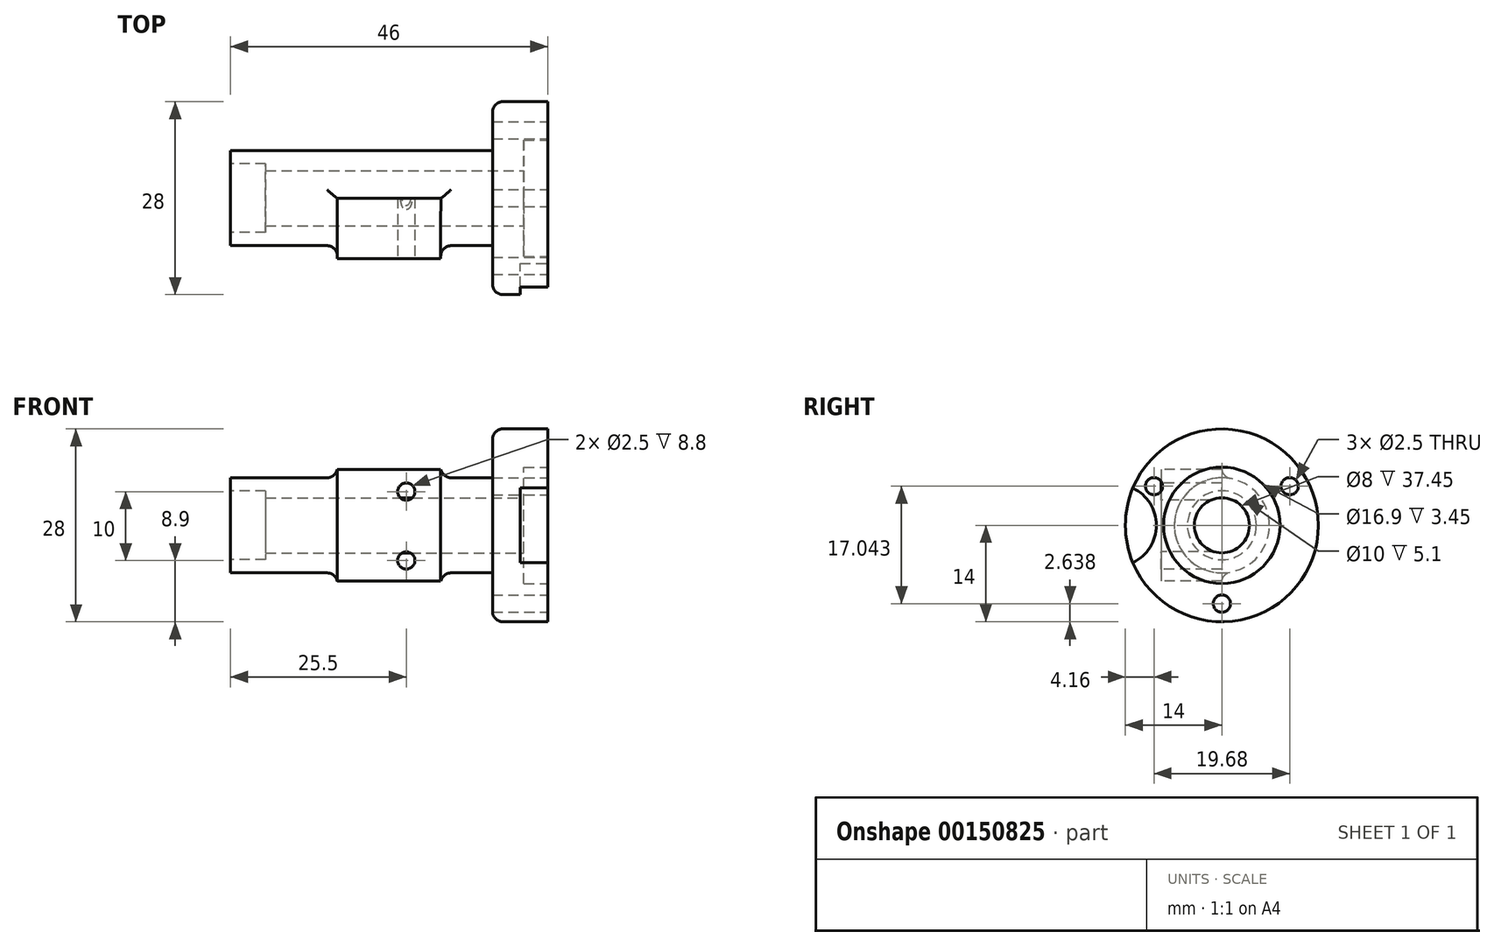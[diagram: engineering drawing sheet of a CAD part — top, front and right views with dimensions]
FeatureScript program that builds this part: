
annotation { "Feature Type Name" : "Feature", "Feature Type Description" : "" }
export const myFeature = defineFeature(function(context is Context, id is Id, definition is map)
    precondition{}
    {
        {
            var Q0;
            Q0=qCreatedBy(makeId("Right.planeOp"),FACE);
            var sketch = newSketch(context, id + "F0", { "sketchPlane" : qUnion([Q0])});
            skCircle(sketch, "E0", {"center": v(0, 0) * mm, "radius": 14 * mm});
            skSolve(sketch);
        }
        {
            var Q0;
            Q0=makeQuery(id+"F0.imprint","IMPRINT",FACE,{"disambiguationData":[TD([[makeQuery(id+"F0.imprint","IMPRINT",EDGE,{"derivedFrom":sQuery(id+"F0.wireOp",EDGE,"E0")}),1.0]])]});
            extrude(context, id + "F1", {"entities" : qUnion([Q0]), "depth" : 8 * mm});
        }
        {
            var Q0;
            Q0=makeQuery(id+"F1.opExtrude","CAP_FACE",FACE,{"disambiguationData":[OSD([sQuery(id+"F0.wireOp",EDGE,"E0")])],"isStart":false});
            var sketch = newSketch(context, id + "F2", { "sketchPlane" : qUnion([Q0])});
            skCircle(sketch, "E1", {"center": v(0, 0) * mm, "radius": 8.45 * mm});
            skSolve(sketch);
        }
        {
            var Q0;
            Q0=qSketchRegion(id+"F2",true);
            extrude(context, id + "F3", {"entities" : qUnion([Q0]), "operationType" : NewBodyOperationType.REMOVE, "oppositeDirection" : true, "depth" : 3.45 * mm});
        }
        {
            var Q0;
            Q0=makeQuery(id+"F1.opExtrude","CAP_FACE",FACE,{"disambiguationData":[OSD([sQuery(id+"F0.wireOp",EDGE,"E0")])],"isStart":false});
            var sketch = newSketch(context, id + "F4", { "sketchPlane" : qUnion([Q0])});
            skCircle(sketch, "E2", {"center": v(0, 0) * mm, "radius": 11.36 * mm, "construction": true});
            skCircle(sketch, "E3", {"center": v(0, -11.36) * mm, "radius": 1.25 * mm});
            skCircle(sketch, "E4.1.0", {"center": v(9.84, 5.68) * mm, "radius": 1.25 * mm});
            skCircle(sketch, "E4.2.0", {"center": v(-9.84, 5.68) * mm, "radius": 1.25 * mm});
            skSolve(sketch);
        }
        {
            var Q0;
            Q0=makeQuery(id+"F4.imprint","IMPRINT",FACE,{"disambiguationData":[TD([[makeQuery(id+"F4.imprint","IMPRINT",EDGE,{"derivedFrom":sQuery(id+"F4.wireOp",EDGE,"E4.2.0")}),1.0]])]});
            var Q1;
            Q1=makeQuery(id+"F4.imprint","IMPRINT",FACE,{"disambiguationData":[TD([[makeQuery(id+"F4.imprint","IMPRINT",EDGE,{"derivedFrom":sQuery(id+"F4.wireOp",EDGE,"E4.1.0")}),1.0]])]});
            var Q2;
            Q2=makeQuery(id+"F4.imprint","IMPRINT",FACE,{"disambiguationData":[TD([[makeQuery(id+"F4.imprint","IMPRINT",EDGE,{"derivedFrom":sQuery(id+"F4.wireOp",EDGE,"E3")}),1.0]])]});
            extrude(context, id + "F5", {"entities" : qUnion([Q0, Q1, Q2]), "operationType" : NewBodyOperationType.REMOVE, "endBound" : BoundingType.THROUGH_ALL, "oppositeDirection" : true, "depth" : 25 * mm});
        }
        {
            var Q0;
            Q0=makeQuery(id+"F1.opExtrude","CAP_FACE",FACE,{"disambiguationData":[OSD([sQuery(id+"F0.wireOp",EDGE,"E0")])],"isStart":true});
            var sketch = newSketch(context, id + "F6", { "sketchPlane" : qUnion([Q0])});
            skCircle(sketch, "E5", {"center": v(0, 0) * mm, "radius": 6.9 * mm});
            skSolve(sketch);
        }
        {
            var Q0;
            Q0=makeQuery(id+"F6.imprint","IMPRINT",FACE,{"disambiguationData":[TD([[makeQuery(id+"F6.imprint","IMPRINT",EDGE,{"derivedFrom":sQuery(id+"F6.wireOp",EDGE,"E5")}),1.0]])]});
            extrude(context, id + "F7", {"entities" : qUnion([Q0]), "operationType" : NewBodyOperationType.ADD, "depth" : 38 * mm});
        }
        {
            var Q0;
            Q0=qCreatedBy(makeId("Top.planeOp"),FACE);
            var sketch = newSketch(context, id + "F8", { "sketchPlane" : qUnion([Q0])});
            skLineSegment(sketch, "E6.bottom", {"start": v(-22.5, 0) * mm, "end": v(-7.5, 0) * mm});
            skLineSegment(sketch, "E6.top", {"start": v(-22.5, -8.8) * mm, "end": v(-7.5, -8.8) * mm});
            skLineSegment(sketch, "E6.left", {"start": v(-22.5, 0) * mm, "end": v(-22.5, -8.8) * mm});
            skLineSegment(sketch, "E6.right", {"start": v(-7.5, 0) * mm, "end": v(-7.5, -8.8) * mm});
            skSolve(sketch);
        }
        {
            var Q0;
            Q0=makeQuery(id+"F8.imprint","IMPRINT",FACE,{"disambiguationData":[TD([[makeQuery(id+"F8.imprint","IMPRINT",EDGE,{"derivedFrom":sQuery(id+"F8.wireOp",EDGE,"E6.bottom")}),-1.0]])]});
            extrude(context, id + "F9", {"entities" : qUnion([Q0]), "operationType" : NewBodyOperationType.ADD, "endBound" : BoundingType.SYMMETRIC, "depth" : 16.2 * mm});
        }
        {
            var Q0;
            Q0=makeQuery(id+"F1.opExtrude","CAP_FACE",FACE,{"disambiguationData":[OSD([sQuery(id+"F0.wireOp",EDGE,"E0")])],"isStart":false});
            var sketch = newSketch(context, id + "F10", { "sketchPlane" : qUnion([Q0])});
            skCircle(sketch, "E7", {"center": v(0, 0) * mm, "radius": 4 * mm});
            skSolve(sketch);
        }
        {
            var Q0;
            Q0=makeQuery(id+"F10.imprint","IMPRINT",FACE,{"disambiguationData":[TD([[makeQuery(id+"F10.imprint","IMPRINT",EDGE,{"derivedFrom":sQuery(id+"F10.wireOp",EDGE,"E7")}),1.0]])]});
            extrude(context, id + "F11", {"entities" : qUnion([Q0]), "operationType" : NewBodyOperationType.REMOVE, "endBound" : BoundingType.THROUGH_ALL, "oppositeDirection" : true, "depth" : 25 * mm});
        }
        {
            var Q0;
            Q0=makeQuery(id+"F7.opExtrude","CAP_FACE",FACE,{"disambiguationData":[OSD([sQuery(id+"F6.wireOp",EDGE,"E5")])],"isStart":false});
            var sketch = newSketch(context, id + "F12", { "sketchPlane" : qUnion([Q0])});
            skCircle(sketch, "E8", {"center": v(0, 0) * mm, "radius": 5 * mm});
            skSolve(sketch);
        }
        {
            var Q0;
            Q0=makeQuery(id+"F12.imprint","IMPRINT",FACE,{"disambiguationData":[TD([[makeQuery(id+"F12.imprint","IMPRINT",EDGE,{"derivedFrom":sQuery(id+"F12.wireOp",EDGE,"E8")}),1.0]])]});
            extrude(context, id + "F13", {"entities" : qUnion([Q0]), "operationType" : NewBodyOperationType.REMOVE, "oppositeDirection" : true, "depth" : 5.1 * mm});
        }
        {
            var Q0;
            Q0=makeQuery(id+"F9.opExtrude","SWEPT_FACE",FACE,{"disambiguationData":[OSD([sQuery(id+"F8.wireOp",EDGE,"E6.top")])]});
            var sketch = newSketch(context, id + "F14", { "sketchPlane" : qUnion([Q0])});
            skCircle(sketch, "E9", {"center": v(-12.5, -5.1) * mm, "radius": 1.25 * mm});
            skLineSegment(sketch, "E10", {"start": v(-12.5, -16.17) * mm, "end": v(-12.5, 16.97) * mm, "construction": true});
            skCircle(sketch, "E11", {"center": v(-12.5, 4.9) * mm, "radius": 1.25 * mm});
            skSolve(sketch);
        }
        {
            var Q0;
            Q0=makeQuery(id+"F14.imprint","IMPRINT",FACE,{"disambiguationData":[TD([[makeQuery(id+"F14.imprint","IMPRINT",EDGE,{"derivedFrom":sQuery(id+"F14.wireOp",EDGE,"E11")}),1.0]])]});
            var Q1;
            Q1=makeQuery(id+"F14.imprint","IMPRINT",FACE,{"disambiguationData":[TD([[makeQuery(id+"F14.imprint","IMPRINT",EDGE,{"derivedFrom":sQuery(id+"F14.wireOp",EDGE,"E9")}),1.0]])]});
            extrude(context, id + "F15", {"entities" : qUnion([Q0, Q1]), "operationType" : NewBodyOperationType.REMOVE, "oppositeDirection" : true, "depth" : 8.8 * mm});
        }
        {
            var Q0;
            Q0=makeQuery(id+"F1.opExtrude","CAP_FACE",FACE,{"disambiguationData":[OSD([sQuery(id+"F0.wireOp",EDGE,"E0")])],"isStart":false});
            var sketch = newSketch(context, id + "F16", { "sketchPlane" : qUnion([Q0])});
            skCircle(sketch, "E12", {"center": v(-15.5, 0) * mm, "radius": 6 * mm});
            skSolve(sketch);
        }
        {
            var Q0;
            Q0=qSketchRegion(id+"F16",true);
            extrude(context, id + "F17", {"entities" : qUnion([Q0]), "operationType" : NewBodyOperationType.REMOVE, "oppositeDirection" : true, "depth" : 4 * mm});
        }
        {
            var Q0;
            Q0=makeQuery(id+"F7.opExtrude","CAP_EDGE",EDGE,{"disambiguationData":[OSD([sQuery(id+"F6.wireOp",EDGE,"E5")])],"isStart":true});
            var Q1;
            Q1=makeQuery(id+"F9.boolean.opBoolean","INTERSECT",EDGE,{"derivedFrom":[makeQuery(id+"F7.opExtrude","SWEPT_FACE",FACE,{"disambiguationData":[OSD([sQuery(id+"F6.wireOp",EDGE,"E5")])]}),makeQuery(id+"F9.opExtrude","SWEPT_FACE",FACE,{"disambiguationData":[OSD([sQuery(id+"F8.wireOp",EDGE,"E6.left")])]})]});
            var Q2;
            Q2=makeQuery(id+"F9.boolean.opBoolean","INTERSECT",EDGE,{"derivedFrom":[makeQuery(id+"F7.opExtrude","SWEPT_FACE",FACE,{"disambiguationData":[OSD([sQuery(id+"F6.wireOp",EDGE,"E5")])]}),makeQuery(id+"F9.opExtrude","SWEPT_FACE",FACE,{"disambiguationData":[OSD([sQuery(id+"F8.wireOp",EDGE,"E6.right")])]})]});
            var Q3;
            Q3=makeQuery(id+"F9.boolean.opBoolean","INTERSECT",EDGE,{"disambiguationData":[OD(1.0)],"derivedFrom":[makeQuery(id+"F7.opExtrude","SWEPT_FACE",FACE,{"disambiguationData":[OSD([sQuery(id+"F6.wireOp",EDGE,"E5")])]}),makeQuery(id+"F9.opExtrude","SWEPT_FACE",FACE,{"disambiguationData":[OSD([sQuery(id+"F8.wireOp",EDGE,"E6.bottom")])]})]});
            var Q4;
            Q4=makeQuery(id+"F9.boolean.opBoolean","INTERSECT",EDGE,{"disambiguationData":[OD(0.0)],"derivedFrom":[makeQuery(id+"F7.opExtrude","SWEPT_FACE",FACE,{"disambiguationData":[OSD([sQuery(id+"F6.wireOp",EDGE,"E5")])]}),makeQuery(id+"F9.opExtrude","SWEPT_FACE",FACE,{"disambiguationData":[OSD([sQuery(id+"F8.wireOp",EDGE,"E6.bottom")])]})]});
            fillet(context, id + "F18", {"entities" : qUnion([Q0, Q1, Q2, Q3, Q4]), "radius" : 1.5 * mm, "tangentPropagation" : true, "allowEdgeOverflow" : false});
        }
        {
            var Q0;
            Q0=makeQuery(id+"F1.opExtrude","CAP_EDGE",EDGE,{"disambiguationData":[OSD([sQuery(id+"F0.wireOp",EDGE,"E0")])],"isStart":true});
            fillet(context, id + "F19", {"entities" : qUnion([Q0]), "radius" : 1.5 * mm, "tangentPropagation" : true, "allowEdgeOverflow" : false});
        }
    });
